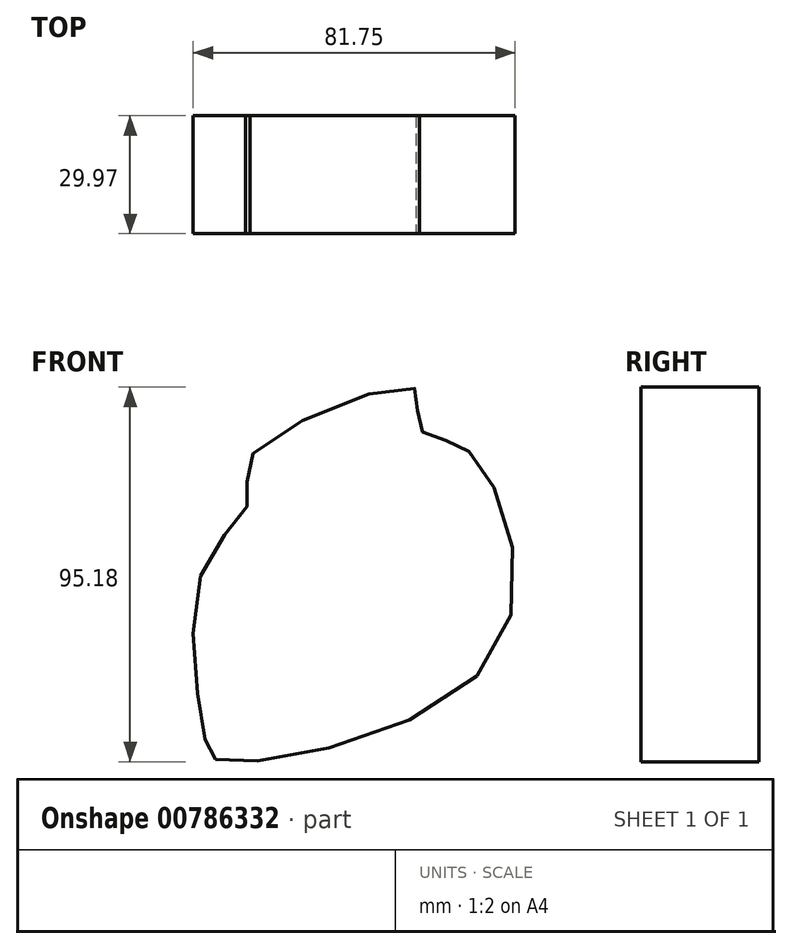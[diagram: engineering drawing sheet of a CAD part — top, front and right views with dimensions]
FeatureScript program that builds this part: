
annotation { "Feature Type Name" : "Feature", "Feature Type Description" : "" }
export const myFeature = defineFeature(function(context is Context, id is Id, definition is map)
    precondition{}
    {
        {
            var Q0;
            Q0=qCreatedBy(makeId("Front.planeOp"),FACE);
            var sketch = newSketch(context, id + "F0", { "sketchPlane" : qUnion([Q0])});
            skFitSpline(sketch, "E0", {"points": [v(-53.64, -43) * mm, v(-54.2, 0) * mm, v(-42.28, 18.21) * mm, v(-42.28, 28.43) * mm, v(0, 45.93) * mm, v(0, 37.65) * mm, v(6, 33.28) * mm, v(15.08, 28.52) * mm, v(19.62, -21.85) * mm, v(-49.1, -48.5) * mm, v(-53.64, -43) * mm]});
            skSolve(sketch);
        }
        {
            var Q0;
            Q0=makeQuery(id+"F0.imprint","IMPRINT",FACE,{"disambiguationData":[TD([[makeQuery(id+"F0.imprint","IMPRINT",EDGE,{"derivedFrom":sQuery(id+"F0.wireOp",EDGE,"E0")}),-1.0]])]});
            extrude(context, id + "F1", {"entities" : qUnion([Q0]), "oppositeDirection" : true, "depth" : 29.97 * mm, "offsetDistance" : 25.4 * mm});
        }
    });
